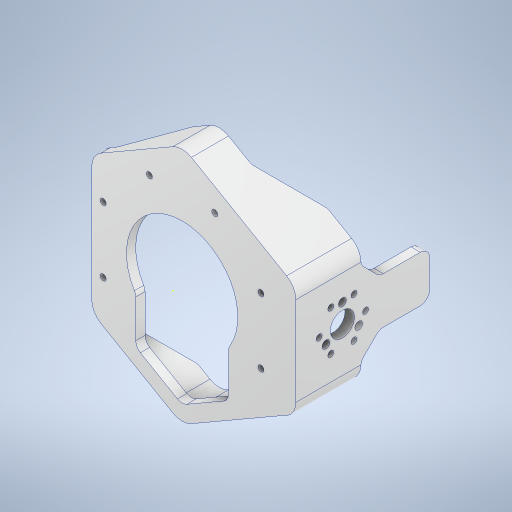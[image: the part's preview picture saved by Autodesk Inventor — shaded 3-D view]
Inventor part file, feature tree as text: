
AUTODESK INVENTOR PART (.ipt)
format: ipt  version: 2024.3 (Build 283343000, 343)  size: 740,352 bytes
history: native  units: mm
features: sketch x17, extrude x13, hole x3, fillet x3, projected_geometry x3, other x1, mirror x1
ambient origin geometry x8: Origin, YZ Plane, XZ Plane, XY Plane, X Axis, Y Axis, Z Axis, Center Point
bodies: Body1 (feature_tree)
feature tree (41):
  other  "ソリッド1"
  extrude  "押し出し1"  Depth=5.0mm TaperAngle=0.0deg
  hole  "穴1"  [1 undecoded]
  extrude  "押し出し2"  TaperAngle=22.5deg  [1 undecoded]
  extrude  "押し出し13"  Depth=80.0mm TaperAngle=360.0deg
  hole  "穴5"  [1 undecoded]
  hole  "穴6"  [1 undecoded]
  extrude  "押し出し14"  Depth=50.0mm
  extrude  "押し出し21"  Depth=65.0mm
  sketch  "スケッチ35"
  extrude  "押し出し28"  Depth=60.0mm TaperAngle=360.0deg
  extrude  "押し出し31"  Depth=65.0mm
  extrude  "押し出し32"  Depth=50.0mm
  extrude  "押し出し33"  Depth=65.0mm
  extrude  "押し出し34"  Depth=5.0mm TaperAngle=0.0deg
  extrude  "押し出し35"  Depth=60.0mm TaperAngle=360.0deg
  fillet  "フィレット28"  Radius=25.0mm
  fillet  "フィレット29"  [1 undecoded]
  extrude  "押し出し36"  Depth=30.0mm TaperAngle=360.0deg
  fillet  "フィレット31"  Radius=25.0mm
  mirror  "ミラー1"
  extrude  "押し出し37"  TaperAngle=0.0deg  [1 undecoded]
  sketch  "スケッチ1"
  sketch  "スケッチ2"
  sketch  "スケッチ3"
  sketch  "スケッチ17"
  sketch  "スケッチ18"
  sketch  "スケッチ19"
  sketch  "スケッチ20"
  sketch  "スケッチ28"
  sketch  "スケッチ36"
  projected_geometry  "投影ループ1"
  sketch  "スケッチ39"
  sketch  "スケッチ40"
  sketch  "スケッチ42"
  sketch  "スケッチ43"
  sketch  "スケッチ45"
  projected_geometry  "投影ループ2"
  sketch  "スケッチ46"
  projected_geometry  "投影ループ3"
  sketch  "スケッチ47"
note: 6 required parameter values undecoded (feature->parameter linkage not recoverable at this tier; creation-order binding heuristic only, values carry confidence <= 0.55)
